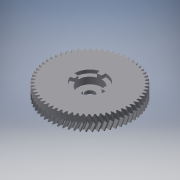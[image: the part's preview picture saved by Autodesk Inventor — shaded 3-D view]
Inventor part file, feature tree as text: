
AUTODESK INVENTOR PART (.ipt)
format: ipt  version: 2017 (Build 210142000, 142)  size: 1,468,928 bytes
history: native  units: mm
features: sketch x5, extrude x5, pattern_circular x3, helix x2, projected_geometry x1
ambient origin geometry x8: Origin, YZ Plane, XZ Plane, XY Plane, X Axis, Y Axis, Z Axis, Center Point
bodies: Solid1 (feature_tree)
feature tree (16):
  sketch  "Sketch1"  dims[d0=20.0mm d1=0.0mm]
  extrude  "Extrusion1"  TaperAngle=0.0deg  [1 undecoded]
  extrude  "Extrusion2"  Depth=610.0mm TaperAngle=360.0deg
  pattern_circular  "Circular Pattern1"  [2 undecoded]
  extrude  "Extrusion3"  Depth=6.0mm
  extrude  "Extrusion4"  Depth=12.217305mm
  extrude  "Extrusion5"  Depth=5.0mm TaperAngle=0.0deg
  pattern_circular  "Circular Pattern2"  Count=4 Angle=360.0deg
  helix  "Coil1"  [1 undecoded]
  helix  "Coil2"  [1 undecoded]
  pattern_circular  "Circular Pattern3"  [2 undecoded]
  sketch  "Sketch2"  dims[d2=10.0mm d3=0.0mm d4=610.0mm d5=360.0deg]
  sketch  "Sketch3"  dims[d7=13.5mm]
  sketch  "Sketch4"  dims[d8=10.0mm d9=0.0mm]
  sketch  "Sketch5"  dims[d10=35.0mm d11=15.0mm d12=0.0mm d13=6.0mm d14=12.217305mm d15=5.0mm d16=0.0mm d17=40.0mm d18=360.0deg d20=10.0mm d21=10.0mm d22=0.1mm d23=0.0mm d24=90.0deg d25=90.0deg d26=0.0mm d27=0.0mm d28=10.0mm d29=10.0mm d30=0.1mm d31=0.0mm d32=90.0deg d33=90.0deg d34=0.0mm d35=0.0mm d36=610.0mm d37=360.0deg]
  projected_geometry  "Projected Loop1"
note: 7 required parameter values undecoded (feature->parameter linkage not recoverable at this tier; creation-order binding heuristic only, values carry confidence <= 0.55)
